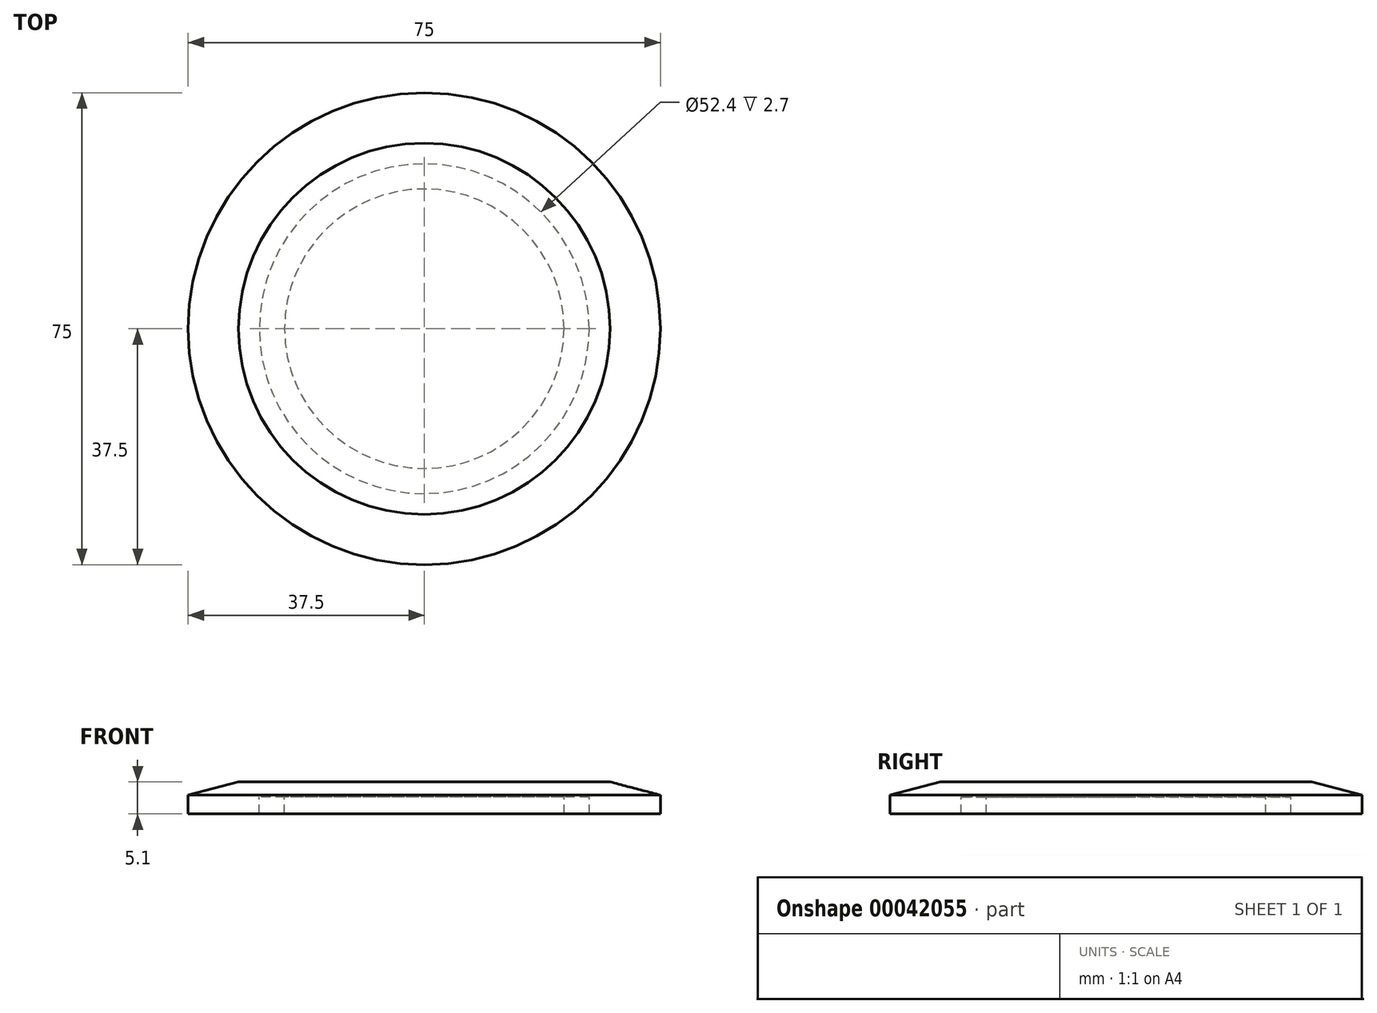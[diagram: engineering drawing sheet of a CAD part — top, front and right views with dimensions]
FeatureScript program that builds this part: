
annotation { "Feature Type Name" : "Feature", "Feature Type Description" : "" }
export const myFeature = defineFeature(function(context is Context, id is Id, definition is map)
    precondition{}
    {
        {
            var Q0;
            Q0=qCreatedBy(makeId("Front.planeOp"),FACE);
            var sketch = newSketch(context, id + "F0", { "sketchPlane" : qUnion([Q0])});
            skLineSegment(sketch, "E0", {"start": v(0, 0) * mm, "end": v(0, 5.1) * mm, "construction": true});
            skLineSegment(sketch, "E1", {"start": v(0, 0) * mm, "end": v(22.2, 0) * mm});
            skLineSegment(sketch, "E2", {"start": v(37.5, 0) * mm, "end": v(37.5, 3) * mm});
            skLineSegment(sketch, "E3", {"start": v(37.5, 3) * mm, "end": v(29.5, 5.1) * mm});
            skLineSegment(sketch, "E4", {"start": v(29.5, 5.1) * mm, "end": v(0, 5.1) * mm});
            skLineSegment(sketch, "E5", {"start": v(22.2, 0) * mm, "end": v(22.2, 2.7) * mm});
            skLineSegment(sketch, "E6", {"start": v(22.2, 2.7) * mm, "end": v(26.2, 2.7) * mm});
            skLineSegment(sketch, "E7", {"start": v(26.2, 2.7) * mm, "end": v(26.2, 0) * mm});
            skLineSegment(sketch, "E8.trimOffspring", {"start": v(26.2, 0) * mm, "end": v(37.5, 0) * mm});
            skLineSegment(sketch, "E9", {"start": v(0, 5.1) * mm, "end": v(0, 0) * mm});
            skSolve(sketch);
        }
        {
            var Q0;
            Q0=makeQuery(id+"F0.imprint","IMPRINT",FACE,{"disambiguationData":[TD([[makeQuery(id+"F0.imprint","IMPRINT",EDGE,{"derivedFrom":sQuery(id+"F0.wireOp",EDGE,"E1")}),1.0]])]});
            var Q1;
            Q1=sQuery(id+"F0.wireOp",EDGE,"E9");
            revolve(context, id + "F1", {"entities" : qUnion([Q0]), "axis" : qUnion([Q1]), "revolveType" : RevolveType.FULL});
        }
    });
